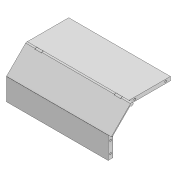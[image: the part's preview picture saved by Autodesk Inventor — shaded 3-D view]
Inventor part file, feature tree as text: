
AUTODESK INVENTOR PART (.ipt)
format: ipt  version: 2020 (Build 240168000, 168)  size: 632,320 bytes
history: native  units: mm
features: sketch x20, extrude x19, projected_geometry x16, chamfer x2
ambient origin geometry x8: Origin, YZ Plane, XZ Plane, XY Plane, X Axis, Y Axis, Z Axis, Center Point
bodies: Solid1 (feature_tree)
feature tree (57):
  extrude  "Extrusion1"  Depth=120.0mm
  extrude  "Extrusion2"  Depth=40.0mm
  extrude  "Extrusion3"  TaperAngle=135.0deg  [1 undecoded]
  extrude  "Extrusion4"  Depth=5.0mm
  extrude  "Extrusion5"  Depth=1.0mm
  extrude  "Extrusion6"  Depth=20.0mm
  extrude  "Extrusion7"  Depth=10.0mm TaperAngle=0.0deg
  extrude  "Extrusion8"  Depth=0.3mm
  extrude  "Extrusion9"  Depth=0.25mm
  extrude  "Extrusion10"  Depth=0.25mm
  extrude  "Extrusion11"  Depth=0.3mm
  extrude  "Extrusion17"  Depth=20.0mm TaperAngle=0.0deg
  extrude  "Extrusion18"  Depth=5.0mm
  extrude  "Extrusion19"  Depth=0.35mm TaperAngle=0.0deg
  extrude  "Extrusion20"  Depth=0.25mm
  extrude  "Extrusion21"  Depth=0.3mm
  extrude  "Extrusion22"  Depth=0.3mm
  extrude  "Extrusion23"  Depth=0.3mm
  extrude  "Extrusion24"  Depth=0.3mm
  sketch  "Sketch25"  dims[d73=0.3mm d74=5.0mm d75=0.25mm d76=19.547688mm d77=0.35mm d78=0.0mm d79=0.3mm d80=5.0mm d81=0.25mm d82=19.547688mm d83=20.0mm d84=0.0mm d96=3.0mm d107=10.0mm d108=0.0mm d109=12.0mm d110=10.0mm d111=0.0mm d112=10.0mm d113=0.0mm d114=12.0mm d115=5.5mm d116=3.25mm d117=10.0mm d118=0.0mm d119=6.0mm d120=15.0mm d121=6.0mm d122=15.0mm d123=6.0mm d124=6.0mm d125=15.0mm d126=15.0mm d127=4.0mm d128=0.0mm d129=4.2mm d130=4.2mm d131=4.2mm d132=4.2mm d133=3.0mm d134=0.0mm d135=6.0mm d136=6.0mm d137=15.0mm d138=15.0mm d139=4.0mm d140=0.0mm d141=4.2mm d142=4.2mm d143=3.0mm d144=0.0mm d145=2.0mm d146=4.0mm d147=45.0deg d148=2.0mm d149=4.0mm d150=45.0deg d17=0.872665mm]
  chamfer  "Chamfer1"  Distance=20.0mm
  chamfer  "Chamfer2"  Distance=0.35mm
  sketch  "Sketch1"  dims[d0=55.0mm d1=120.0mm]
  sketch  "Sketch2"  dims[d2=50.0mm d3=40.0mm]
  projected_geometry  "Projected Loop1"
  sketch  "Sketch3"  dims[d4=135.0deg d5=135.0deg]
  sketch  "Sketch4"  dims[d6=5.0mm d7=125.0mm]
  projected_geometry  "Projected Loop2"
  projected_geometry  "Projected Loop3"
  sketch  "Sketch5"  dims[d8=190.0mm d9=1.0mm]
  sketch  "Sketch6"  dims[d10=1.0mm d11=20.0mm]
  sketch  "Sketch7"  dims[d12=3.0mm d13=10.0mm d14=0.0mm]
  sketch  "Sketch8"  dims[d15=3.0mm d16=0.3mm]
  sketch  "Sketch9"  dims[d18=5.0mm d19=0.25mm]
  sketch  "Sketch10"  dims[d21=0.25mm d22=0.25mm]
  sketch  "Sketch11"  dims[d23=0.0mm d24=0.0mm d25=0.3mm d26=5.0mm d27=0.25mm]
  sketch  "Sketch17"  dims[d28=2.0mm d29=20.0mm d30=0.0mm]
  projected_geometry  "Projected Loop7"
  sketch  "Sketch18"  dims[d36=5.0mm d37=14.196mm]
  sketch  "Sketch19"  dims[d38=0.3mm d39=5.0mm d40=0.25mm d41=0.35mm d42=0.0mm]
  projected_geometry  "Projected Loop8"
  sketch  "Sketch20"  dims[d43=0.3mm d44=5.0mm d45=0.25mm d46=19.547688mm]
  sketch  "Sketch21"  dims[d47=20.0mm d48=0.0mm d49=0.3mm d50=5.0mm d51=0.25mm d52=19.547688mm]
  projected_geometry  "Projected Loop9"
  projected_geometry  "Projected Loop10"
  sketch  "Sketch22"  dims[d53=0.35mm d54=0.0mm d55=0.3mm d56=5.0mm d57=0.25mm d58=19.547688mm]
  projected_geometry  "Projected Loop11"
  projected_geometry  "Projected Loop12"
  projected_geometry  "Projected Loop13"
  projected_geometry  "Projected Loop14"
  sketch  "Sketch23"  dims[d59=228.6mm d60=0.0mm d61=0.3mm d62=5.0mm d63=0.25mm d64=19.547688mm]
  sketch  "Sketch24"  dims[d65=0.35mm d66=0.0mm d67=0.3mm d68=5.0mm d69=0.25mm d70=19.547688mm d71=20.0mm d72=0.0mm]
  projected_geometry  "Projected Loop15"
  projected_geometry  "Projected Loop16"
  projected_geometry  "Projected Loop17"
  projected_geometry  "Projected Loop18"
  projected_geometry  "Projected Loop19"
note: 1 required parameter value undecoded (feature->parameter linkage not recoverable at this tier; creation-order binding heuristic only, values carry confidence <= 0.55)
